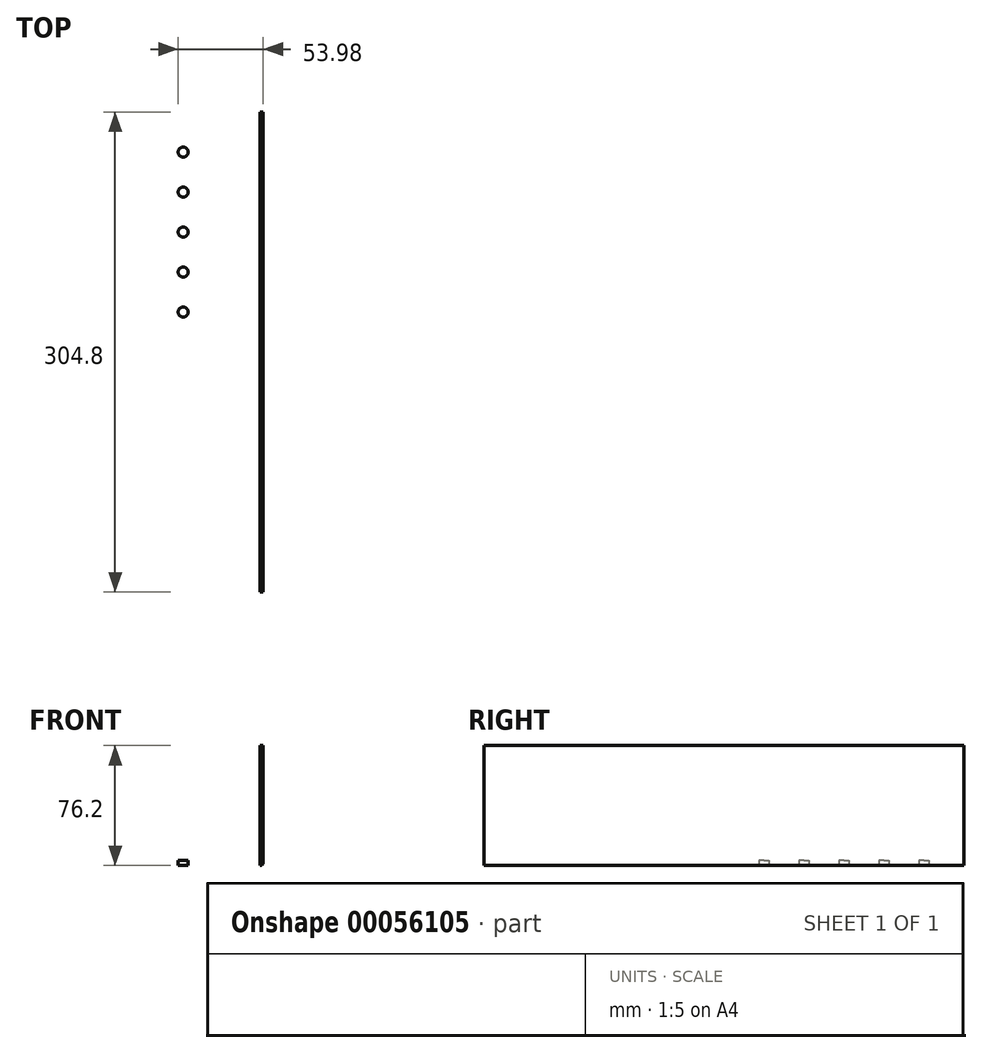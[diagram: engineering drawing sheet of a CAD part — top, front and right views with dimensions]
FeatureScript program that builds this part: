
annotation { "Feature Type Name" : "Feature", "Feature Type Description" : "" }
export const myFeature = defineFeature(function(context is Context, id is Id, definition is map)
    precondition{}
    {
        {
            var Q0;
            Q0=qCreatedBy(makeId("Front.planeOp"),FACE);
            var sketch = newSketch(context, id + "F0", { "sketchPlane" : qUnion([Q0])});
            skLineSegment(sketch, "E0", {"start": v(0, 0) * mm, "end": v(-76.2, 0) * mm});
            skLineSegment(sketch, "E1", {"start": v(-76.2, 0) * mm, "end": v(-76.2, 3.17) * mm});
            skLineSegment(sketch, "E2", {"start": v(-76.2, 3.17) * mm, "end": v(-3.17, 3.17) * mm});
            skLineSegment(sketch, "E3", {"start": v(-3.17, 3.17) * mm, "end": v(-3.17, 76.2) * mm});
            skLineSegment(sketch, "E4", {"start": v(-3.18, 76.2) * mm, "end": v(0, 76.2) * mm});
            skLineSegment(sketch, "E5", {"start": v(0, 76.2) * mm, "end": v(0, 0) * mm});
            skCircle(sketch, "E6", {"center": v(-5.03, 5.03) * mm, "radius": 1.86 * mm});
            skCircle(sketch, "E7", {"center": v(-1.86, 1.86) * mm, "radius": 1.86 * mm});
            skSolve(sketch);
        }
        {
            var Q0;
            {var subQ4=sQuery(id+"F0.wireOp",EDGE,"E1");Q0=makeQuery(id+"F0.imprint","IMPRINT",FACE,{"disambiguationData":[TD([[makeQuery(id+"F0.imprint","IMPRINT",EDGE,{"derivedFrom":subQ4}),-1.0]])]});}
            var Q1;
            {var subQ1=sQuery(id+"F0.wireOp",EDGE,"E4");Q1=makeQuery(id+"F0.imprint","IMPRINT",FACE,{"disambiguationData":[TD([[makeQuery(id+"F0.imprint","IMPRINT",EDGE,{"derivedFrom":subQ1}),-1.0]])]});}
            var Q2;
            {var subQ1=sQuery(id+"F0.wireOp",EDGE,"E2");var subQ3=sQuery(id+"F0.wireOp",EDGE,"E6");var subQ4=makeQuery(id+"F0.imprint","INTERSECT",VERTEX,{"derivedFrom":[subQ1,subQ3]});Q2=makeQuery(id+"F0.imprint","IMPRINT",FACE,{"disambiguationData":[TD([[makeQuery(id+"F0.imprint","IMPRINT",EDGE,{"disambiguationData":[TD([[subQ4,-1.0]])],"derivedFrom":subQ3}),-1.0]])]});}
            var Q3;
            {var subQ0=sQuery(id+"F0.wireOp",EDGE,"E7");var subQ3=makeQuery(id+"F0.imprint","INTERSECT",VERTEX,{"derivedFrom":[sQuery(id+"F0.wireOp",EDGE,"E0"),subQ0]});Q3=makeQuery(id+"F0.imprint","IMPRINT",FACE,{"disambiguationData":[TD([[makeQuery(id+"F0.imprint","IMPRINT",EDGE,{"disambiguationData":[TD([[subQ3,-1.0]])],"derivedFrom":subQ0}),1.0]])]});}
            extrude(context, id + "F1", {"entities" : qUnion([Q0, Q1, Q2, Q3]), "depth" : 304.8 * mm});
        }
        {
            var Q0;
            Q0=makeQuery(id+"F1.opExtrude","SWEPT_FACE",FACE,{"disambiguationData":[OSD([sQuery(id+"F0.wireOp",EDGE,"E5")])]});
            var sketch = newSketch(context, id + "F2", { "sketchPlane" : qUnion([Q0])});
            skLineSegment(sketch, "E8", {"start": v(-152.4, 76.2) * mm, "end": v(-152.4, 0) * mm, "construction": true});
            skLineSegment(sketch, "E9.0", {"start": v(-304.8, 76.2) * mm, "end": v(0, 76.2) * mm});
            skLineSegment(sketch, "E9.1", {"start": v(-304.8, 76.2) * mm, "end": v(-304.8, 1.86) * mm});
            skLineSegment(sketch, "E9.2", {"start": v(-304.8, 1.86) * mm, "end": v(0, 1.86) * mm});
            skLineSegment(sketch, "E9.3", {"start": v(0, 76.2) * mm, "end": v(0, 1.86) * mm});
            skCircle(sketch, "E10", {"center": v(-152.4, 50.8) * mm, "radius": 3.18 * mm});
            skCircle(sketch, "E11.1.0.0", {"center": v(-127, 50.8) * mm, "radius": 3.18 * mm});
            skCircle(sketch, "E11.2.0.0", {"center": v(-101.6, 50.8) * mm, "radius": 3.18 * mm});
            skCircle(sketch, "E11.3.0.0", {"center": v(-76.2, 50.8) * mm, "radius": 3.18 * mm});
            skCircle(sketch, "E11.4.0.0", {"center": v(-50.8, 50.8) * mm, "radius": 3.18 * mm});
            skCircle(sketch, "E11.5.0.0", {"center": v(-25.4, 50.8) * mm, "radius": 3.18 * mm});
            skLineSegment(sketch, "E11.direction1", {"start": v(-152.4, 50.8) * mm, "end": v(-127, 50.8) * mm, "construction": true});
            skCircle(sketch, "E12.MirrorC", {"center": v(-177.8, 50.8) * mm, "radius": 3.18 * mm});
            skCircle(sketch, "E13.MirrorC", {"center": v(-203.2, 50.8) * mm, "radius": 3.18 * mm});
            skCircle(sketch, "E14.MirrorC", {"center": v(-228.6, 50.8) * mm, "radius": 3.18 * mm});
            skCircle(sketch, "E15.MirrorC", {"center": v(-254, 50.8) * mm, "radius": 3.18 * mm});
            skCircle(sketch, "E16.MirrorC", {"center": v(-279.4, 50.8) * mm, "radius": 3.18 * mm});
            skSolve(sketch);
        }
        {
            var Q0;
            Q0=makeQuery(id+"F1.opExtrude","SWEPT_FACE",FACE,{"disambiguationData":[OSD([sQuery(id+"F0.wireOp",EDGE,"E0")])]});
            var sketch = newSketch(context, id + "F3", { "sketchPlane" : qUnion([Q0])});
            skLineSegment(sketch, "E17", {"start": v(-1.86, 152.4) * mm, "end": v(-76.2, 152.4) * mm, "construction": true});
            skLineSegment(sketch, "E18.0", {"start": v(-1.86, 304.8) * mm, "end": v(-1.86, 0) * mm});
            skLineSegment(sketch, "E18.1", {"start": v(-1.86, 304.8) * mm, "end": v(-76.2, 304.8) * mm});
            skLineSegment(sketch, "E18.2", {"start": v(-1.86, 0) * mm, "end": v(-76.2, 0) * mm});
            skLineSegment(sketch, "E18.3", {"start": v(-76.2, 304.8) * mm, "end": v(-76.2, 0) * mm});
            skCircle(sketch, "E19", {"center": v(-50.8, 152.4) * mm, "radius": 3.18 * mm});
            skCircle(sketch, "E20.0.1.0", {"center": v(-50.8, 177.8) * mm, "radius": 3.18 * mm});
            skCircle(sketch, "E20.0.2.0", {"center": v(-50.8, 203.2) * mm, "radius": 3.18 * mm});
            skCircle(sketch, "E20.0.3.0", {"center": v(-50.8, 228.6) * mm, "radius": 3.18 * mm});
            skCircle(sketch, "E20.0.4.0", {"center": v(-50.8, 254) * mm, "radius": 3.18 * mm});
            skCircle(sketch, "E20.0.5.0", {"center": v(-50.8, 279.4) * mm, "radius": 3.18 * mm});
            skLineSegment(sketch, "E20.direction1", {"start": v(-50.8, 152.4) * mm, "end": v(-25.4, 152.4) * mm, "construction": true});
            skLineSegment(sketch, "E20.direction2", {"start": v(-50.8, 152.4) * mm, "end": v(-50.8, 177.8) * mm, "construction": true});
            skCircle(sketch, "E21.MirrorC", {"center": v(-50.8, 127) * mm, "radius": 3.18 * mm});
            skCircle(sketch, "E22.MirrorC", {"center": v(-50.8, 101.6) * mm, "radius": 3.18 * mm});
            skCircle(sketch, "E23.MirrorC", {"center": v(-50.8, 76.2) * mm, "radius": 3.18 * mm});
            skCircle(sketch, "E24.MirrorC", {"center": v(-50.8, 50.8) * mm, "radius": 3.18 * mm});
            skCircle(sketch, "E25.MirrorC", {"center": v(-50.8, 25.4) * mm, "radius": 3.18 * mm});
            skSolve(sketch);
        }
        {
            var Q0;
            Q0=makeQuery(id+"F3.imprint","IMPRINT",FACE,{"disambiguationData":[TD([[makeQuery(id+"F3.imprint","IMPRINT",EDGE,{"derivedFrom":sQuery(id+"F3.wireOp",EDGE,"E20.0.5.0")}),1.0]])]});
            var Q1;
            Q1=makeQuery(id+"F3.imprint","IMPRINT",FACE,{"disambiguationData":[TD([[makeQuery(id+"F3.imprint","IMPRINT",EDGE,{"derivedFrom":sQuery(id+"F3.wireOp",EDGE,"E20.0.4.0")}),1.0]])]});
            var Q2;
            Q2=makeQuery(id+"F3.imprint","IMPRINT",FACE,{"disambiguationData":[TD([[makeQuery(id+"F3.imprint","IMPRINT",EDGE,{"derivedFrom":sQuery(id+"F3.wireOp",EDGE,"E20.0.3.0")}),1.0]])]});
            var Q3;
            Q3=makeQuery(id+"F3.imprint","IMPRINT",FACE,{"disambiguationData":[TD([[makeQuery(id+"F3.imprint","IMPRINT",EDGE,{"derivedFrom":sQuery(id+"F3.wireOp",EDGE,"E20.0.2.0")}),1.0]])]});
            var Q4;
            Q4=makeQuery(id+"F3.imprint","IMPRINT",FACE,{"disambiguationData":[TD([[makeQuery(id+"F3.imprint","IMPRINT",EDGE,{"derivedFrom":sQuery(id+"F3.wireOp",EDGE,"E20.0.1.0")}),1.0]])]});
            var Q5;
            Q5=makeQuery(id+"F3.imprint","IMPRINT",FACE,{"disambiguationData":[TD([[makeQuery(id+"F3.imprint","IMPRINT",EDGE,{"derivedFrom":sQuery(id+"F3.wireOp",EDGE,"E19")}),1.0]])]});
            var Q6;
            Q6=makeQuery(id+"F3.imprint","IMPRINT",FACE,{"disambiguationData":[TD([[makeQuery(id+"F3.imprint","IMPRINT",EDGE,{"derivedFrom":sQuery(id+"F3.wireOp",EDGE,"E21.MirrorC")}),-1.0]])]});
            var Q7;
            Q7=makeQuery(id+"F3.imprint","IMPRINT",FACE,{"disambiguationData":[TD([[makeQuery(id+"F3.imprint","IMPRINT",EDGE,{"derivedFrom":sQuery(id+"F3.wireOp",EDGE,"E22.MirrorC")}),-1.0]])]});
            var Q8;
            Q8=makeQuery(id+"F3.imprint","IMPRINT",FACE,{"disambiguationData":[TD([[makeQuery(id+"F3.imprint","IMPRINT",EDGE,{"derivedFrom":sQuery(id+"F3.wireOp",EDGE,"E23.MirrorC")}),-1.0]])]});
            var Q9;
            Q9=makeQuery(id+"F3.imprint","IMPRINT",FACE,{"disambiguationData":[TD([[makeQuery(id+"F3.imprint","IMPRINT",EDGE,{"derivedFrom":sQuery(id+"F3.wireOp",EDGE,"E24.MirrorC")}),-1.0]])]});
            var Q10;
            Q10=makeQuery(id+"F3.imprint","IMPRINT",FACE,{"disambiguationData":[TD([[makeQuery(id+"F3.imprint","IMPRINT",EDGE,{"derivedFrom":sQuery(id+"F3.wireOp",EDGE,"E25.MirrorC")}),-1.0]])]});
            extrude(context, id + "F4", {"entities" : qUnion([Q0, Q1, Q2, Q3, Q4, Q5, Q6, Q7, Q8, Q9, Q10]), "operationType" : NewBodyOperationType.REMOVE, "endBound" : BoundingType.THROUGH_ALL, "oppositeDirection" : true, "depth" : 25.4 * mm});
        }
    });
